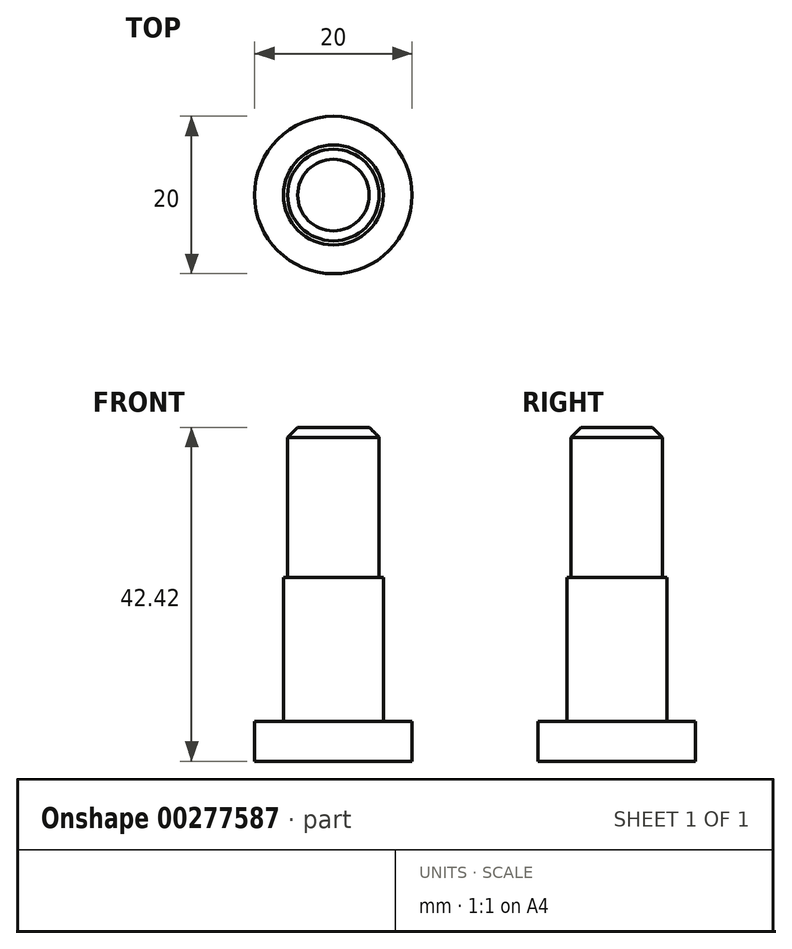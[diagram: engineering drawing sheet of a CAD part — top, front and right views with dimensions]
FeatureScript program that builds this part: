
annotation { "Feature Type Name" : "Feature", "Feature Type Description" : "" }
export const myFeature = defineFeature(function(context is Context, id is Id, definition is map)
    precondition{}
    {
        {
            var Q0;
            Q0=qCreatedBy(makeId("Top.planeOp"),FACE);
            var sketch = newSketch(context, id + "F0", { "sketchPlane" : qUnion([Q0])});
            skCircle(sketch, "E0", {"center": v(0, 0) * mm, "radius": 6.35 * mm});
            skCircle(sketch, "E1", {"center": v(0, 0) * mm, "radius": 10 * mm});
            skCircle(sketch, "E2", {"center": v(0, 0) * mm, "radius": 5.82 * mm});
            skSolve(sketch);
        }
        {
            var Q0;
            Q0=makeQuery(id+"F0.imprint","IMPRINT",FACE,{"disambiguationData":[TD([[makeQuery(id+"F0.imprint","IMPRINT",EDGE,{"derivedFrom":sQuery(id+"F0.wireOp",EDGE,"E0")}),-1.0]])]});
            var Q1;
            Q1=makeQuery(id+"F0.imprint","IMPRINT",FACE,{"disambiguationData":[TD([[makeQuery(id+"F0.imprint","IMPRINT",EDGE,{"derivedFrom":sQuery(id+"F0.wireOp",EDGE,"E0")}),1.0]])]});
            var Q2;
            Q2=makeQuery(id+"F0.imprint","IMPRINT",FACE,{"disambiguationData":[TD([[makeQuery(id+"F0.imprint","IMPRINT",EDGE,{"derivedFrom":sQuery(id+"F0.wireOp",EDGE,"E2")}),1.0]])]});
            extrude(context, id + "F1", {"entities" : qUnion([Q0, Q1, Q2]), "depth" : 5.08 * mm});
        }
        {
            var Q0;
            Q0=makeQuery(id+"F0.imprint","IMPRINT",FACE,{"disambiguationData":[TD([[makeQuery(id+"F0.imprint","IMPRINT",EDGE,{"derivedFrom":sQuery(id+"F0.wireOp",EDGE,"E0")}),1.0]])]});
            var Q1;
            Q1=makeQuery(id+"F0.imprint","IMPRINT",FACE,{"disambiguationData":[TD([[makeQuery(id+"F0.imprint","IMPRINT",EDGE,{"derivedFrom":sQuery(id+"F0.wireOp",EDGE,"E2")}),1.0]])]});
            extrude(context, id + "F2", {"entities" : qUnion([Q0, Q1]), "operationType" : NewBodyOperationType.ADD, "depth" : 23.37 * mm});
        }
        {
            var Q0;
            Q0=makeQuery(id+"F0.imprint","IMPRINT",FACE,{"disambiguationData":[TD([[makeQuery(id+"F0.imprint","IMPRINT",EDGE,{"derivedFrom":sQuery(id+"F0.wireOp",EDGE,"E2")}),1.0]])]});
            extrude(context, id + "F3", {"entities" : qUnion([Q0]), "operationType" : NewBodyOperationType.ADD, "depth" : 42.42 * mm});
        }
        {
            var Q0;
            Q0=makeQuery(id+"F3.opExtrude","CAP_EDGE",EDGE,{"disambiguationData":[OSD([sQuery(id+"F0.wireOp",EDGE,"E2")])],"isStart":false});
            chamfer(context, id + "F4", {"entities" : qUnion([Q0]), "width" : 1.27 * mm, "tangentPropagation" : true});
        }
    });
